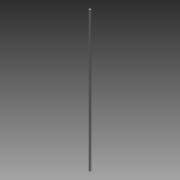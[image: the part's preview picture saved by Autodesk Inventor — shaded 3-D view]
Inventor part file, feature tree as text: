
AUTODESK INVENTOR PART (.ipt)
format: ipt  version: 2015 SP1 (Build 190203100, 203)  size: 65,024 bytes
history: native  units: mm
features: extrude x1, sketch x1
ambient origin geometry x8: Origin, YZ Plane, XZ Plane, XY Plane, X Axis, Y Axis, Z Axis, Center Point
bodies: Solid1 (feature_tree)
feature tree (2):
  extrude  "Extrusion1"  Depth=533.4mm TaperAngle=0.0deg
  sketch  "Sketch1"  dims[d0=8.0mm d1=533.4mm d2=0.0mm]
